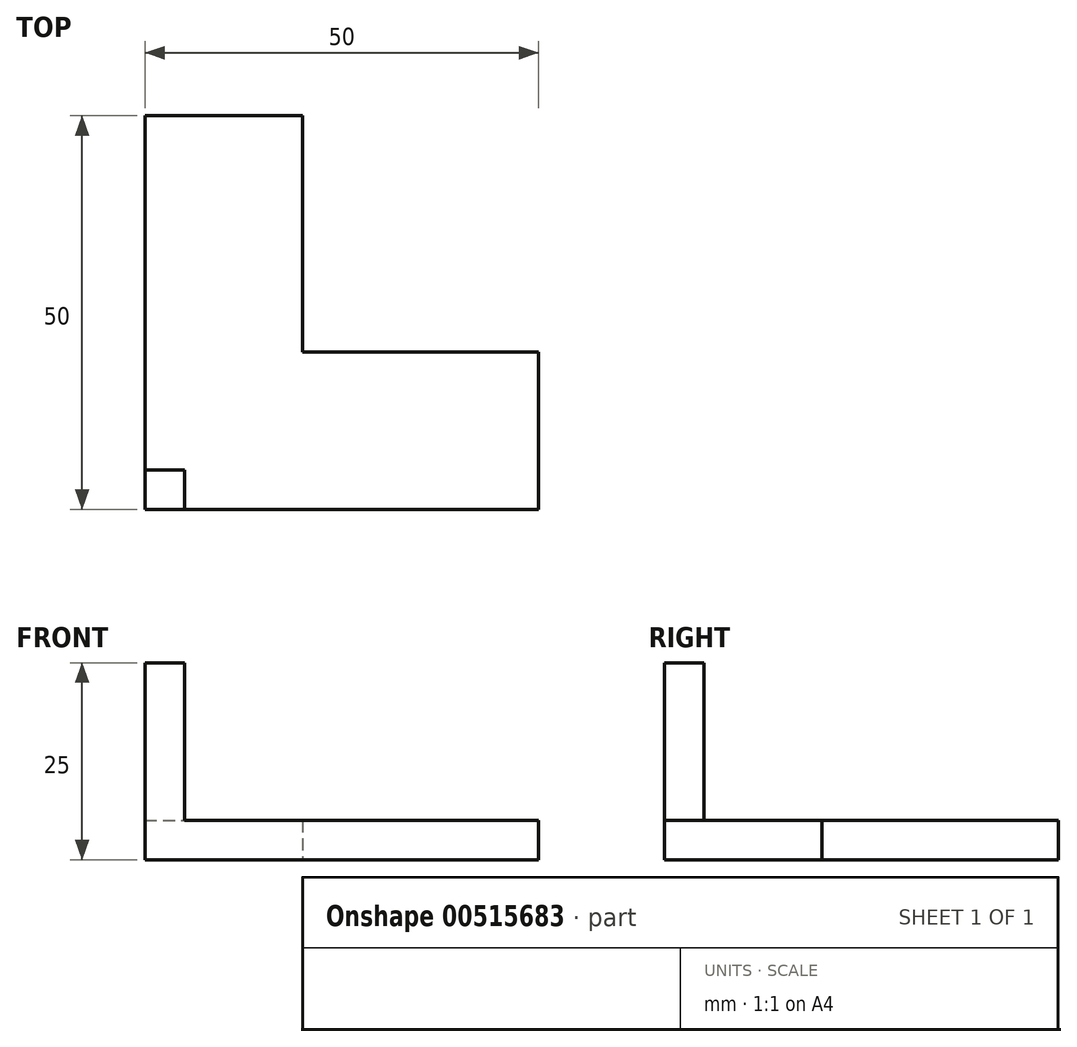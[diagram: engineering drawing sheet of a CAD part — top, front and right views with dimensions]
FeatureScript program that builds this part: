
annotation { "Feature Type Name" : "Feature", "Feature Type Description" : "" }
export const myFeature = defineFeature(function(context is Context, id is Id, definition is map)
    precondition{}
    {
        {
            var Q0;
            Q0=qCreatedBy(makeId("Top.planeOp"),FACE);
            var sketch = newSketch(context, id + "F0", { "sketchPlane" : qUnion([Q0])});
            skLineSegment(sketch, "E0", {"start": v(-25.25, 18.93) * mm, "end": v(-25.25, -31.07) * mm});
            skLineSegment(sketch, "E1", {"start": v(-25.25, 18.93) * mm, "end": v(-5.25, 18.93) * mm});
            skLineSegment(sketch, "E2", {"start": v(-5.25, 18.93) * mm, "end": v(-5.25, -11.07) * mm});
            skLineSegment(sketch, "E3", {"start": v(-5.25, -11.07) * mm, "end": v(24.75, -11.07) * mm});
            skLineSegment(sketch, "E4", {"start": v(24.75, -11.07) * mm, "end": v(24.75, -31.07) * mm});
            skLineSegment(sketch, "E5", {"start": v(24.75, -31.07) * mm, "end": v(-25.25, -31.07) * mm});
            skSolve(sketch);
        }
        {
            var Q0;
            Q0 = qSketchRegion(id + "F0", true);
            extrude(context, id + "F1", {"entities" : qUnion([Q0]), "depth" : 5 * mm, "offsetDistance" : 25 * mm});
        }
        {
            var Q0;
            Q0=makeQuery(id+"F1.opExtrude","CAP_FACE",FACE,{"disambiguationData":[OSD([sQuery(id+"F0.wireOp",EDGE,"E0"),sQuery(id+"F0.wireOp",EDGE,"E1"),sQuery(id+"F0.wireOp",EDGE,"E2"),sQuery(id+"F0.wireOp",EDGE,"E3"),sQuery(id+"F0.wireOp",EDGE,"E4"),sQuery(id+"F0.wireOp",EDGE,"E5")])],"isStart":false});
            var sketch = newSketch(context, id + "F2", { "sketchPlane" : qUnion([Q0])});
            skLineSegment(sketch, "E6", {"start": v(-25.25, -31.07) * mm, "end": v(-25.25, -26.07) * mm});
            skLineSegment(sketch, "E7", {"start": v(-25.25, -26.07) * mm, "end": v(-20.25, -26.07) * mm});
            skLineSegment(sketch, "E8", {"start": v(-20.25, -26.07) * mm, "end": v(-20.25, -31.07) * mm});
            skLineSegment(sketch, "E9", {"start": v(-20.25, -31.07) * mm, "end": v(-25.25, -31.07) * mm});
            skSolve(sketch);
        }
        {
            var Q0;
            Q0 = qSketchRegion(id + "F2", true);
            extrude(context, id + "F3", {"entities" : qUnion([Q0]), "operationType" : NewBodyOperationType.ADD, "depth" : 20 * mm, "offsetDistance" : 25 * mm});
        }
    });
